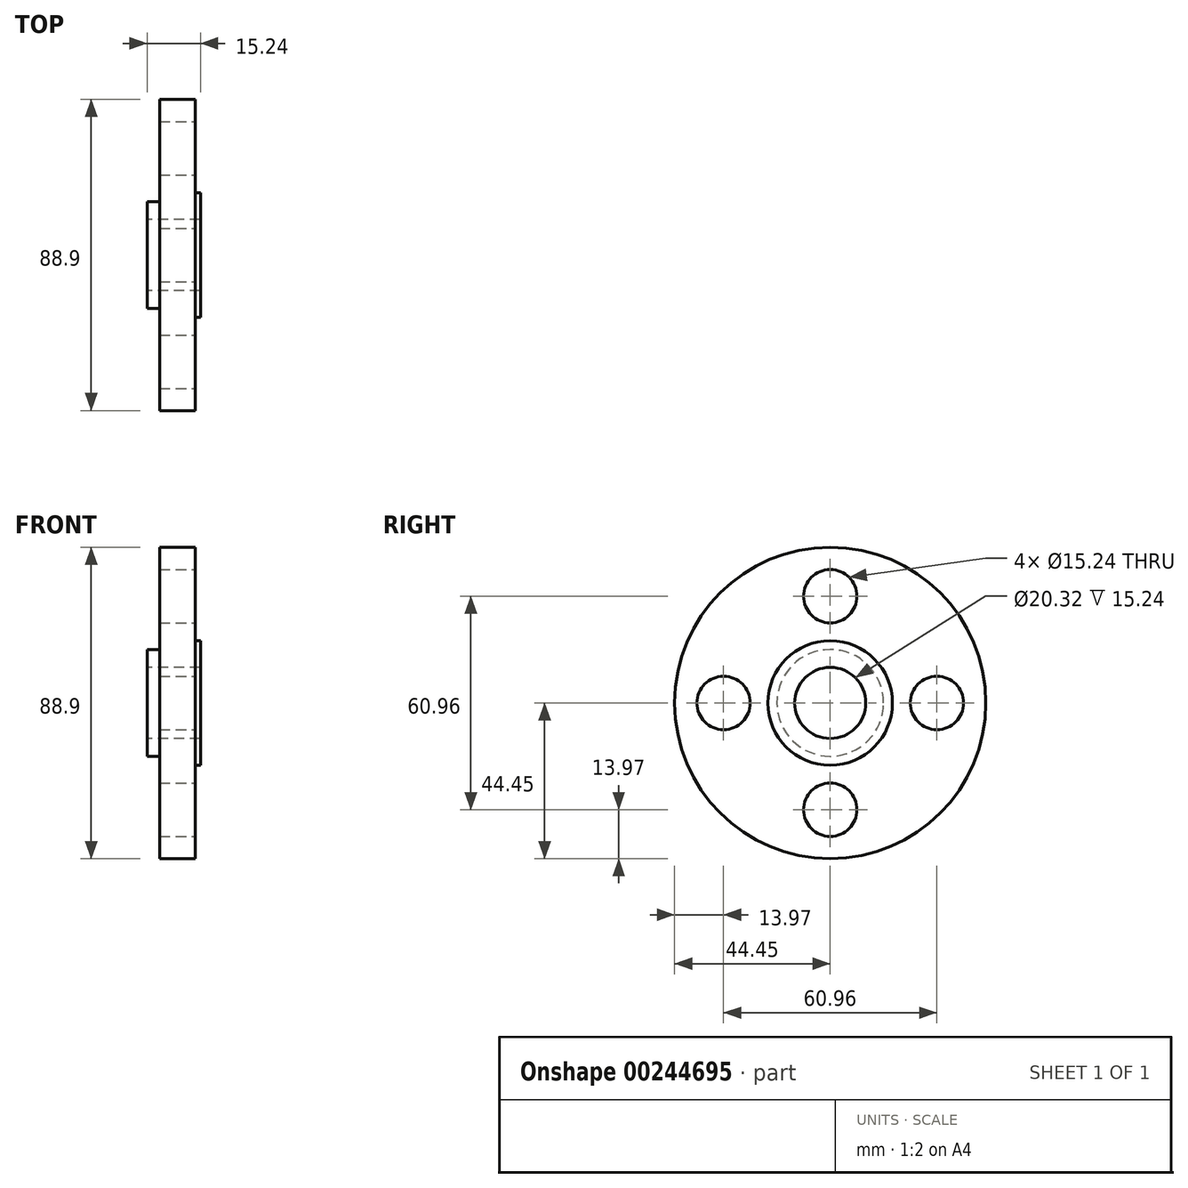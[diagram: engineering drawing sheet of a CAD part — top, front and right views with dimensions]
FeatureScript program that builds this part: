
annotation { "Feature Type Name" : "Feature", "Feature Type Description" : "" }
export const myFeature = defineFeature(function(context is Context, id is Id, definition is map)
    precondition{}
    {
        {
            var Q0;
            Q0=qCreatedBy(makeId("Front.planeOp"),FACE);
            var sketch = newSketch(context, id + "F0", { "sketchPlane" : qUnion([Q0])});
            skLineSegment(sketch, "E0", {"start": v(-142.28, 0) * mm, "end": v(119.13, 0) * mm, "construction": true});
            skLineSegment(sketch, "E1", {"start": v(-30.13, 10.16) * mm, "end": v(-14.89, 10.16) * mm});
            skLineSegment(sketch, "E2", {"start": v(-14.89, 10.16) * mm, "end": v(-14.89, 17.78) * mm});
            skLineSegment(sketch, "E3", {"start": v(-14.89, 17.78) * mm, "end": v(-16.41, 17.78) * mm});
            skLineSegment(sketch, "E4", {"start": v(-16.41, 17.78) * mm, "end": v(-16.41, 44.45) * mm});
            skLineSegment(sketch, "E5", {"start": v(-16.41, 44.45) * mm, "end": v(-26.57, 44.45) * mm});
            skLineSegment(sketch, "E6", {"start": v(-26.57, 44.45) * mm, "end": v(-26.57, 15.24) * mm});
            skLineSegment(sketch, "E7", {"start": v(-26.57, 15.24) * mm, "end": v(-30.13, 15.24) * mm});
            skLineSegment(sketch, "E8", {"start": v(-30.13, 15.24) * mm, "end": v(-30.13, 10.16) * mm});
            skSolve(sketch);
        }
        {
            var Q0;
            Q0=makeQuery(id+"F0.imprint","IMPRINT",FACE,{"disambiguationData":[TD([[makeQuery(id+"F0.imprint","IMPRINT",EDGE,{"derivedFrom":sQuery(id+"F0.wireOp",EDGE,"E1")}),1.0]])]});
            var Q1;
            Q1=sQuery(id+"F0.wireOp",EDGE,"E0");
            revolve(context, id + "F1", {"entities" : qUnion([Q0]), "axis" : qUnion([Q1]), "revolveType" : RevolveType.FULL});
        }
        {
            var Q0;
            Q0=makeQuery(id+"F1.opRevolve","SWEPT_FACE",FACE,{"disambiguationData":[OSD([sQuery(id+"F0.wireOp",EDGE,"E4")])]});
            var sketch = newSketch(context, id + "F2", { "sketchPlane" : qUnion([Q0])});
            skCircle(sketch, "E9", {"center": v(0, 0) * mm, "radius": 30.48 * mm, "construction": true});
            skCircle(sketch, "E10", {"center": v(0, 30.48) * mm, "radius": 7.62 * mm});
            skCircle(sketch, "E11.1.0", {"center": v(-30.48, 0) * mm, "radius": 7.62 * mm});
            skCircle(sketch, "E11.2.0", {"center": v(0, -30.48) * mm, "radius": 7.62 * mm});
            skCircle(sketch, "E11.3.0", {"center": v(30.48, 0) * mm, "radius": 7.62 * mm});
            skSolve(sketch);
        }
        {
            var Q0;
            Q0 = qSketchRegion(id + "F2", true);
            extrude(context, id + "F3", {"entities" : qUnion([Q0]), "operationType" : NewBodyOperationType.REMOVE, "endBound" : BoundingType.THROUGH_ALL, "oppositeDirection" : true, "depth" : 25.4 * mm});
        }
    });
